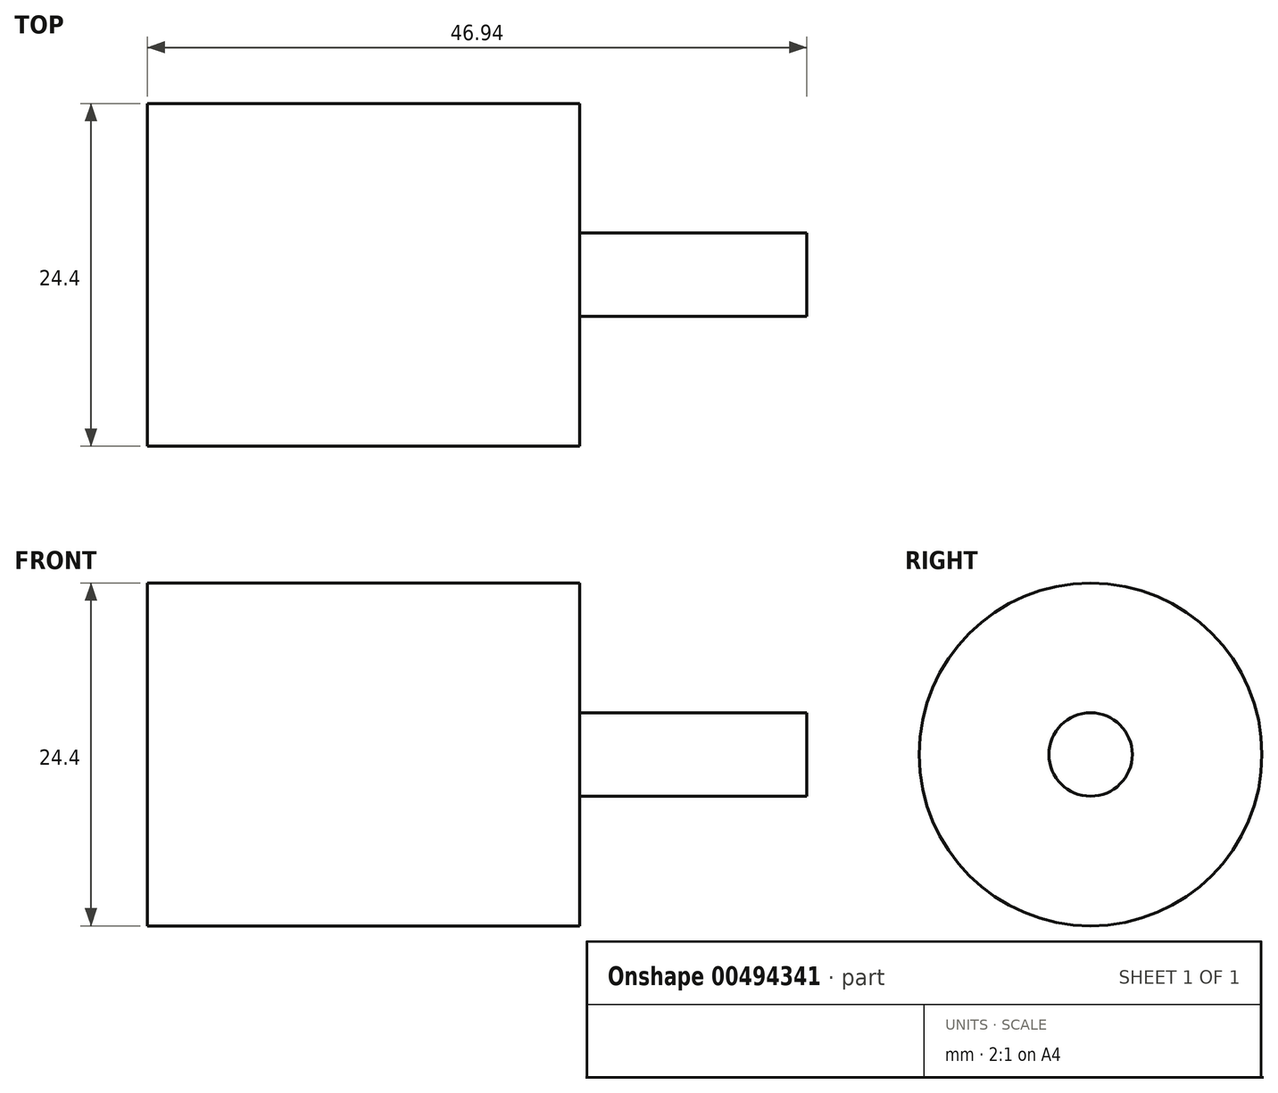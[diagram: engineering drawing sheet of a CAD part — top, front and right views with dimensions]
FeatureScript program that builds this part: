
annotation { "Feature Type Name" : "Feature", "Feature Type Description" : "" }
export const myFeature = defineFeature(function(context is Context, id is Id, definition is map)
    precondition{}
    {
        {
            var Q0;
            Q0=qCreatedBy(makeId("Right.planeOp"),FACE);
            var sketch = newSketch(context, id + "F0", { "sketchPlane" : qUnion([Q0])});
            skCircle(sketch, "E0", {"center": v(0, 0) * mm, "radius": 12.2 * mm});
            skSolve(sketch);
        }
        {
            var Q0;
            Q0=makeQuery(id+"F0.imprint","IMPRINT",FACE,{"disambiguationData":[TD([[makeQuery(id+"F0.imprint","IMPRINT",EDGE,{"derivedFrom":sQuery(id+"F0.wireOp",EDGE,"E0")}),1.0]])]});
            extrude(context, id + "F1", {"entities" : qUnion([Q0]), "depth" : 30.78 * mm, "offsetDistance" : 25 * mm});
        }
        {
            var Q0;
            Q0=makeQuery(id+"F1.opExtrude","CAP_FACE",FACE,{"disambiguationData":[OSD([sQuery(id+"F0.wireOp",EDGE,"E0")])],"isStart":false});
            var sketch = newSketch(context, id + "F2", { "sketchPlane" : qUnion([Q0])});
            skCircle(sketch, "E1", {"center": v(0, 0) * mm, "radius": 2.97 * mm});
            skSolve(sketch);
        }
        {
            var Q0;
            Q0=makeQuery(id+"F2.imprint","IMPRINT",FACE,{"disambiguationData":[TD([[makeQuery(id+"F2.imprint","IMPRINT",EDGE,{"derivedFrom":sQuery(id+"F2.wireOp",EDGE,"E1")}),1.0]])]});
            extrude(context, id + "F3", {"entities" : qUnion([Q0]), "operationType" : NewBodyOperationType.ADD, "depth" : 16.16 * mm, "offsetDistance" : 25 * mm});
        }
    });
